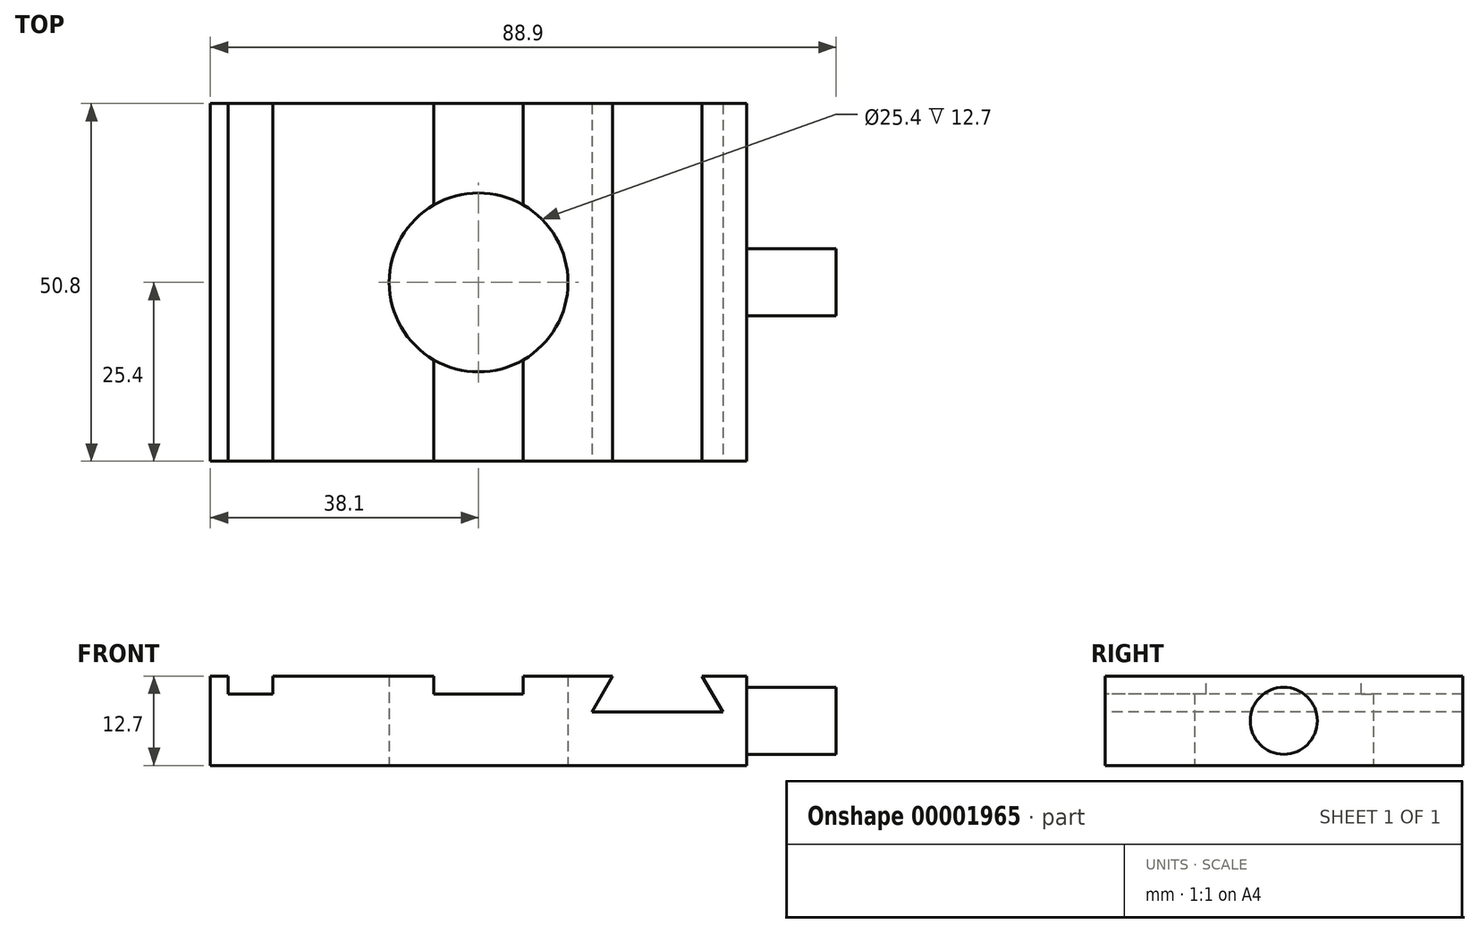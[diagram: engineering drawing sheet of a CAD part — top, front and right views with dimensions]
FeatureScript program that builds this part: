
annotation { "Feature Type Name" : "Feature", "Feature Type Description" : "" }
export const myFeature = defineFeature(function(context is Context, id is Id, definition is map)
    precondition{}
    {
        {
            var Q0;
            Q0=qCreatedBy(makeId("Top.planeOp"),FACE);
            var sketch = newSketch(context, id + "F0", { "sketchPlane" : qUnion([Q0])});
            skLineSegment(sketch, "E0.bottom", {"start": v(38.1, -25.4) * mm, "end": v(-38.1, -25.4) * mm});
            skLineSegment(sketch, "E0.top", {"start": v(38.1, 25.4) * mm, "end": v(-38.1, 25.4) * mm});
            skLineSegment(sketch, "E0.left", {"start": v(38.1, -25.4) * mm, "end": v(38.1, 25.4) * mm});
            skLineSegment(sketch, "E0.right", {"start": v(-38.1, -25.4) * mm, "end": v(-38.1, 25.4) * mm});
            skPoint(sketch, "E0.middle", {"position": v(0, 0) * mm});
            skLineSegment(sketch, "E1", {"start": v(-38.1, 0) * mm, "end": v(38.1, 0) * mm, "construction": true});
            skLineSegment(sketch, "E2", {"start": v(0, 25.4) * mm, "end": v(0, -25.4) * mm, "construction": true});
            skLineSegment(sketch, "E3.MirrorCS", {"start": v(38.1, 0) * mm, "end": v(-38.1, 0) * mm, "construction": true});
            skCircle(sketch, "E4", {"center": v(0, 0) * mm, "radius": 12.7 * mm});
            skSolve(sketch);
        }
        {
            var Q0;
            Q0=makeQuery(id+"F0.imprint","IMPRINT",FACE,{"disambiguationData":[TD([[makeQuery(id+"F0.imprint","IMPRINT",EDGE,{"derivedFrom":sQuery(id+"F0.wireOp",EDGE,"E0.bottom")}),-1.0]])]});
            extrude(context, id + "F1", {"entities" : qUnion([Q0]), "depth" : 12.7 * mm, "offsetDistance" : 25.4 * mm});
        }
        {
            var Q0;
            Q0=makeQuery(id+"F1.opExtrude","CAP_FACE",FACE,{"disambiguationData":[OSD([sQuery(id+"F0.wireOp",EDGE,"E0.bottom"),sQuery(id+"F0.wireOp",EDGE,"E0.top"),sQuery(id+"F0.wireOp",EDGE,"E0.left"),sQuery(id+"F0.wireOp",EDGE,"E0.right"),sQuery(id+"F0.wireOp",EDGE,"E4")])],"isStart":false});
            var sketch = newSketch(context, id + "F2", { "sketchPlane" : qUnion([Q0])});
            skLineSegment(sketch, "E5.bottom", {"start": v(-35.56, 25.4) * mm, "end": v(-29.21, 25.4) * mm});
            skLineSegment(sketch, "E5.top", {"start": v(-35.56, -25.4) * mm, "end": v(-29.21, -25.4) * mm});
            skLineSegment(sketch, "E5.left", {"start": v(-35.56, 25.4) * mm, "end": v(-35.56, -25.4) * mm});
            skLineSegment(sketch, "E5.right", {"start": v(-29.21, 25.4) * mm, "end": v(-29.21, -25.4) * mm});
            skLineSegment(sketch, "E6.bottom", {"start": v(-6.35, 25.4) * mm, "end": v(6.35, 25.4) * mm});
            skLineSegment(sketch, "E6.top", {"start": v(-6.35, -25.4) * mm, "end": v(6.35, -25.4) * mm});
            skLineSegment(sketch, "E6.left", {"start": v(-6.35, 25.4) * mm, "end": v(-6.35, -25.4) * mm});
            skLineSegment(sketch, "E6.right", {"start": v(6.35, 25.4) * mm, "end": v(6.35, -25.4) * mm});
            skLineSegment(sketch, "E7", {"start": v(0, 25.4) * mm, "end": v(0, -25.4) * mm, "construction": true});
            skSolve(sketch);
        }
        {
            var Q0;
            Q0=makeQuery(id+"F2.imprint","IMPRINT",FACE,{"disambiguationData":[TD([[makeQuery(id+"F2.imprint","IMPRINT",EDGE,{"derivedFrom":sQuery(id+"F2.wireOp",EDGE,"E5.bottom")}),1.0]])]});
            var Q1;
            {var subQ0=sQuery(id+"F2.wireOp",EDGE,"E6.bottom");Q1=makeQuery(id+"F2.imprint","IMPRINT",FACE,{"disambiguationData":[TD([[makeQuery(id+"F2.imprint","IMPRINT",EDGE,{"derivedFrom":subQ0}),1.0]])]});}
            var Q2;
            {var subQ0=sQuery(id+"F2.wireOp",EDGE,"E6.top");Q2=makeQuery(id+"F2.imprint","IMPRINT",FACE,{"disambiguationData":[TD([[makeQuery(id+"F2.imprint","IMPRINT",EDGE,{"derivedFrom":subQ0}),-1.0]])]});}
            extrude(context, id + "F3", {"entities" : qUnion([Q0, Q1, Q2]), "operationType" : NewBodyOperationType.REMOVE, "oppositeDirection" : true, "depth" : 2.54 * mm, "offsetDistance" : 25.4 * mm});
        }
        {
            var Q0;
            Q0=makeQuery(id+"F1.opExtrude","SWEPT_FACE",FACE,{"disambiguationData":[OSD([sQuery(id+"F0.wireOp",EDGE,"E0.bottom")])]});
            var sketch = newSketch(context, id + "F4", { "sketchPlane" : qUnion([Q0])});
            skLineSegment(sketch, "E8", {"start": v(19.05, 12.7) * mm, "end": v(16.12, 7.62) * mm});
            skLineSegment(sketch, "E9", {"start": v(16.12, 7.62) * mm, "end": v(34.68, 7.62) * mm});
            skLineSegment(sketch, "E10", {"start": v(34.68, 7.62) * mm, "end": v(31.75, 12.7) * mm});
            skLineSegment(sketch, "E11", {"start": v(31.75, 12.7) * mm, "end": v(19.05, 12.7) * mm});
            skLineSegment(sketch, "E12", {"start": v(25.4, 7.62) * mm, "end": v(25.4, 12.7) * mm, "construction": true});
            skPoint(sketch, "E12.endSnap0", {"position": v(22.23, 12.7) * mm});
            skSolve(sketch);
        }
        {
            var Q0;
            Q0 = qSketchRegion(id + "F4", true);
            extrude(context, id + "F5", {"entities" : qUnion([Q0]), "operationType" : NewBodyOperationType.REMOVE, "endBound" : BoundingType.UP_TO_NEXT, "oppositeDirection" : true, "depth" : 25.4 * mm, "offsetDistance" : 25.4 * mm});
        }
        {
            var Q0;
            Q0=makeQuery(id+"F1.opExtrude","SWEPT_FACE",FACE,{"disambiguationData":[OSD([sQuery(id+"F0.wireOp",EDGE,"E0.left")])]});
            var sketch = newSketch(context, id + "F6", { "sketchPlane" : qUnion([Q0])});
            skCircle(sketch, "E13", {"center": v(0, 6.35) * mm, "radius": 4.76 * mm});
            skPoint(sketch, "E13.centerSnap0", {"position": v(-25.4, 6.35) * mm});
            skPoint(sketch, "E14", {"position": v(0, 12.7) * mm});
            skSolve(sketch);
        }
        {
            var Q0;
            Q0=makeQuery(id+"F6.imprint","IMPRINT",FACE,{"disambiguationData":[TD([[makeQuery(id+"F6.imprint","IMPRINT",EDGE,{"derivedFrom":sQuery(id+"F6.wireOp",EDGE,"E13")}),1.0]])]});
            extrude(context, id + "F7", {"entities" : qUnion([Q0]), "operationType" : NewBodyOperationType.ADD, "depth" : 12.7 * mm, "offsetDistance" : 25.4 * mm});
        }
    });
